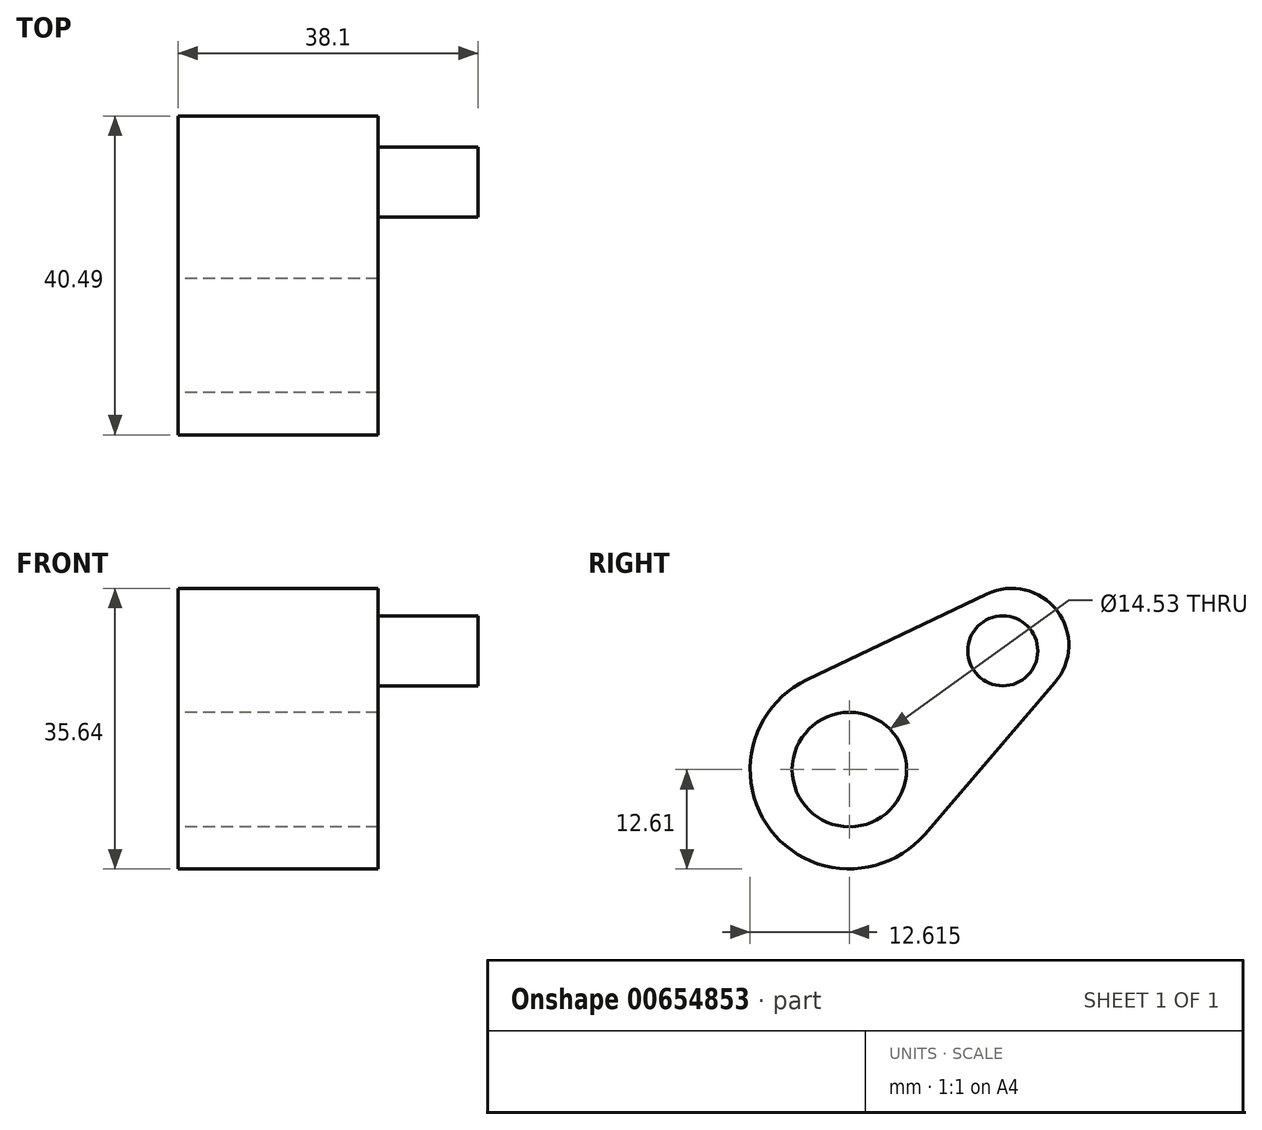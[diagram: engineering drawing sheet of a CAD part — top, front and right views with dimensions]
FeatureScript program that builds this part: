
annotation { "Feature Type Name" : "Feature", "Feature Type Description" : "" }
export const myFeature = defineFeature(function(context is Context, id is Id, definition is map)
    precondition{}
    {
        {
            var Q0;
            Q0=qCreatedBy(makeId("Right.planeOp"),FACE);
            var sketch = newSketch(context, id + "F0", { "sketchPlane" : qUnion([Q0])});
            skCircle(sketch, "E0", {"center": v(-31.62, -19.37) * mm, "radius": 12.61 * mm});
            skCircle(sketch, "E1", {"center": v(-11, -3.6) * mm, "radius": 7.25 * mm});
            skLineSegment(sketch, "E2", {"start": v(-14.12, 2.95) * mm, "end": v(-37.05, -7.99) * mm});
            skLineSegment(sketch, "E3", {"start": v(-22.05, -27.59) * mm, "end": v(-5.5, -8.32) * mm});
            skCircle(sketch, "E4", {"center": v(-31.62, -19.37) * mm, "radius": 7.26 * mm});
            skSolve(sketch);
        }
        {
            var Q0;
            {var subQ0=sQuery(id+"F0.wireOp",EDGE,"E0");var subQ1=makeQuery(id+"F0.imprint","INTERSECT",VERTEX,{"derivedFrom":[subQ0,sQuery(id+"F0.wireOp",EDGE,"E2")]});Q0=makeQuery(id+"F0.imprint","IMPRINT",FACE,{"disambiguationData":[TD([[makeQuery(id+"F0.imprint","IMPRINT",EDGE,{"disambiguationData":[TD([[subQ1,-1.0]])],"derivedFrom":subQ0}),1.0]])]});}
            var Q1;
            {var subQ0=sQuery(id+"F0.wireOp",EDGE,"E2");Q1=makeQuery(id+"F0.imprint","IMPRINT",FACE,{"disambiguationData":[TD([[makeQuery(id+"F0.imprint","IMPRINT",EDGE,{"derivedFrom":subQ0}),1.0]])]});}
            var Q2;
            {var subQ0=sQuery(id+"F0.wireOp",EDGE,"E1");var subQ1=makeQuery(id+"F0.imprint","INTERSECT",VERTEX,{"derivedFrom":[subQ0,sQuery(id+"F0.wireOp",EDGE,"E2")]});Q2=makeQuery(id+"F0.imprint","IMPRINT",FACE,{"disambiguationData":[TD([[makeQuery(id+"F0.imprint","IMPRINT",EDGE,{"disambiguationData":[TD([[subQ1,-1.0]])],"derivedFrom":subQ0}),1.0]])]});}
            extrude(context, id + "F1", {"entities" : qUnion([Q0, Q1, Q2]), "depth" : 25.4 * mm, "offsetDistance" : 25.4 * mm});
        }
        {
            var Q0;
            Q0=qCreatedBy(makeId("Right.planeOp"),FACE);
            var sketch = newSketch(context, id + "F2", { "sketchPlane" : qUnion([Q0])});
            skCircle(sketch, "E5", {"center": v(-12.13, -4.28) * mm, "radius": 4.45 * mm});
            skSolve(sketch);
        }
        {
            var Q0;
            Q0=makeQuery(id+"F2.imprint","IMPRINT",FACE,{"disambiguationData":[TD([[makeQuery(id+"F2.imprint","IMPRINT",EDGE,{"derivedFrom":sQuery(id+"F2.wireOp",EDGE,"E5")}),1.0]])]});
            extrude(context, id + "F3", {"entities" : qUnion([Q0]), "operationType" : NewBodyOperationType.ADD, "depth" : 38.1 * mm, "offsetDistance" : 25.4 * mm});
        }
    });
